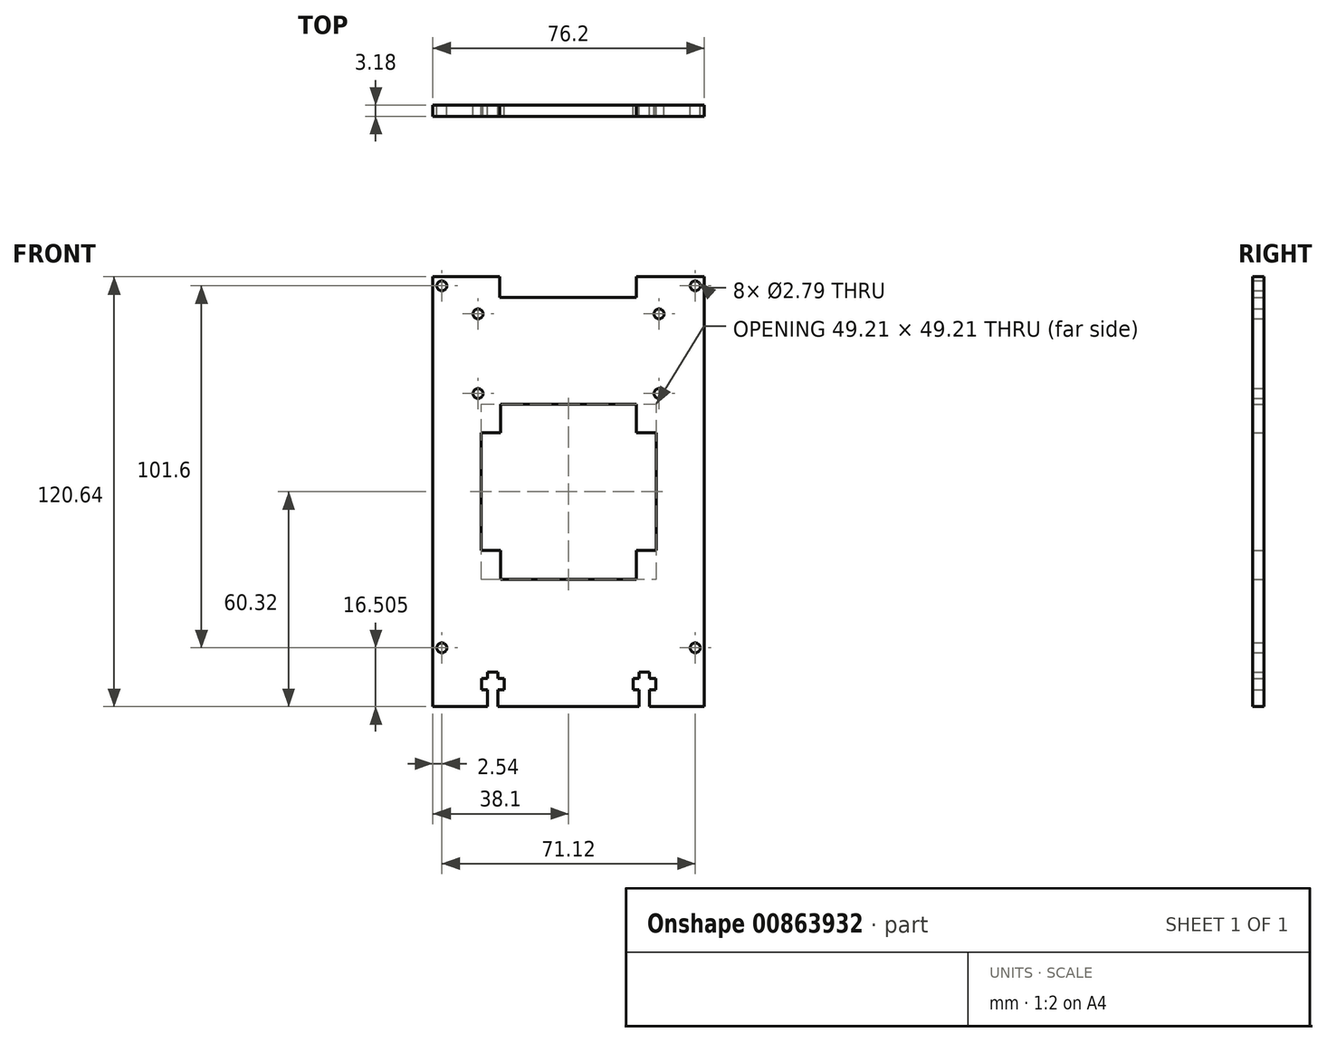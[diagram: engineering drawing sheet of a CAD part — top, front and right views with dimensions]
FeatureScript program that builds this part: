
annotation { "Feature Type Name" : "Feature", "Feature Type Description" : "" }
export const myFeature = defineFeature(function(context is Context, id is Id, definition is map)
    precondition{}
    {
        {
            var Q0;
            Q0=qCreatedBy(makeId("Front.planeOp"),FACE);
            var sketch = newSketch(context, id + "F0", { "sketchPlane" : qUnion([Q0])});
            skLineSegment(sketch, "E0.bottom", {"start": v(38.1, 60.33) * mm, "end": v(-38.1, 60.32) * mm});
            skLineSegment(sketch, "E0.top", {"start": v(38.1, -60.32) * mm, "end": v(-38.1, -60.33) * mm});
            skLineSegment(sketch, "E0.left", {"start": v(38.1, 60.33) * mm, "end": v(38.1, -60.33) * mm});
            skLineSegment(sketch, "E0.right", {"start": v(-38.1, 60.32) * mm, "end": v(-38.1, -60.33) * mm});
            skPoint(sketch, "E0.middle", {"position": v(0, 0) * mm});
            skLineSegment(sketch, "E1.bottom", {"start": v(19.05, 24.6) * mm, "end": v(-19.05, 24.6) * mm});
            skLineSegment(sketch, "E1.top", {"start": v(19.05, -24.6) * mm, "end": v(-19.05, -24.6) * mm});
            skLineSegment(sketch, "E1.left", {"start": v(19.05, 24.6) * mm, "end": v(19.05, -24.6) * mm});
            skLineSegment(sketch, "E1.right", {"start": v(-19.05, 24.6) * mm, "end": v(-19.05, -24.6) * mm});
            skLineSegment(sketch, "E2.bottom", {"start": v(-22.72, -50.67) * mm, "end": v(-19.8, -50.67) * mm});
            skLineSegment(sketch, "E3.bottom", {"start": v(-24.43, -55.56) * mm, "end": v(-18.08, -55.56) * mm});
            skLineSegment(sketch, "E3.top", {"start": v(-24.43, -52.39) * mm, "end": v(-18.08, -52.39) * mm});
            skLineSegment(sketch, "E3.left", {"start": v(-24.43, -55.56) * mm, "end": v(-24.43, -52.39) * mm});
            skLineSegment(sketch, "E3.right", {"start": v(-18.08, -55.56) * mm, "end": v(-18.08, -52.39) * mm});
            skPoint(sketch, "E3.middle", {"position": v(-21.26, -53.98) * mm});
            skLineSegment(sketch, "E4", {"start": v(-22.72, -50.67) * mm, "end": v(-22.72, -60.33) * mm});
            skLineSegment(sketch, "E5", {"start": v(-19.8, -50.67) * mm, "end": v(-19.8, -60.33) * mm});
            skLineSegment(sketch, "E6.bottom", {"start": v(24.6, 16.51) * mm, "end": v(-24.6, 16.51) * mm});
            skLineSegment(sketch, "E6.top", {"start": v(24.6, -16.51) * mm, "end": v(-24.6, -16.51) * mm});
            skLineSegment(sketch, "E6.left", {"start": v(24.6, 16.51) * mm, "end": v(24.6, -16.51) * mm});
            skLineSegment(sketch, "E6.right", {"start": v(-24.6, 16.51) * mm, "end": v(-24.6, -16.51) * mm});
            skLineSegment(sketch, "E7.bottom", {"start": v(-19.28, 60.33) * mm, "end": v(19.05, 60.33) * mm});
            skLineSegment(sketch, "E7.top", {"start": v(-19.28, 54.48) * mm, "end": v(19.05, 54.48) * mm});
            skLineSegment(sketch, "E7.left", {"start": v(-19.28, 60.33) * mm, "end": v(-19.28, 54.48) * mm});
            skLineSegment(sketch, "E7.right", {"start": v(19.05, 60.33) * mm, "end": v(19.05, 54.48) * mm});
            skCircle(sketch, "E8", {"center": v(35.56, 57.79) * mm, "radius": 1.4 * mm});
            skCircle(sketch, "E9", {"center": v(35.56, -43.81) * mm, "radius": 1.4 * mm});
            skLineSegment(sketch, "E10", {"start": v(35.56, 57.79) * mm, "end": v(35.56, 38.74) * mm, "construction": true});
            skLineSegment(sketch, "E11", {"start": v(38.1, 38.74) * mm, "end": v(25.4, 38.74) * mm});
            skCircle(sketch, "E12", {"center": v(25.4, 49.91) * mm, "radius": 1.4 * mm});
            skCircle(sketch, "E13", {"center": v(25.4, 27.56) * mm, "radius": 1.4 * mm});
            skLineSegment(sketch, "E14.MirrorCS", {"start": v(22.72, -50.67) * mm, "end": v(19.8, -50.67) * mm});
            skLineSegment(sketch, "E15.MirrorCS", {"start": v(24.43, -55.56) * mm, "end": v(24.43, -52.39) * mm});
            skLineSegment(sketch, "E16.MirrorCS", {"start": v(19.8, -50.67) * mm, "end": v(19.8, -60.33) * mm});
            skLineSegment(sketch, "E17.MirrorCS", {"start": v(24.43, -55.56) * mm, "end": v(18.08, -55.56) * mm});
            skPoint(sketch, "E18.MirrorP", {"position": v(21.26, -53.98) * mm});
            skLineSegment(sketch, "E19.MirrorCS", {"start": v(22.72, -50.67) * mm, "end": v(22.72, -60.33) * mm});
            skLineSegment(sketch, "E20.MirrorCS", {"start": v(18.08, -55.56) * mm, "end": v(18.08, -52.39) * mm});
            skLineSegment(sketch, "E21.MirrorCS", {"start": v(24.43, -52.39) * mm, "end": v(18.08, -52.39) * mm});
            skCircle(sketch, "E22.MirrorC", {"center": v(-35.56, -43.81) * mm, "radius": 1.4 * mm});
            skCircle(sketch, "E23.MirrorC", {"center": v(-35.56, 57.79) * mm, "radius": 1.4 * mm});
            skCircle(sketch, "E24.MirrorC", {"center": v(-25.4, 49.91) * mm, "radius": 1.4 * mm});
            skCircle(sketch, "E25.MirrorC", {"center": v(-25.4, 27.56) * mm, "radius": 1.4 * mm});
            skSolve(sketch);
        }
        {
            var Q0;
            {var subQ20=sQuery(id+"F0.wireOp",EDGE,"E0.left");Q0=makeQuery(id+"F0.imprint","IMPRINT",FACE,{"disambiguationData":[TD([[makeQuery(id+"F0.imprint","IMPRINT",EDGE,{"derivedFrom":subQ20}),-1.0]])]});}
            extrude(context, id + "F1", {"entities" : qUnion([Q0]), "depth" : 3.17 * mm, "offsetDistance" : 25.4 * mm});
        }
    });
